# Revit family: LOROWERK 21712-050X
name_source: partatom
category: Sanitärinstallationen
revit_build: Autodesk Revit 2017 (Build: 20160225_1515(x64)
units: mm (PartAtom-declared; Revit-internal decimal feet)

## family parameters
Arbeitsebenenbasiert = Nein
Beim Laden mit Abzugskörper schneiden = Nein
Bemaßung runder Anschluss = Durchmesser verwenden
Gemeinsam genutzt = Nein
Immer vertikal = Ja
Raumberechnungspunkt = Nein
Teiletyp = Normal

## types (1)
- LOROWERK 21712-050X
    Abdichtung Grundkörper = mit Klemmflansch (Pressdichtungsflansch)
    Ablaufanschluss Text = mittig
    Anschluss an GLT, GA = Nein
    Begleitheizung = ohne Begleitheizung
    Beschreibung = LORO-DRAINLET DL Flachdachabläufe, einteilig
    Brandschutz mit Klasse R 120 nachrüstbar = Nein
    CONNECTOR0_DIAMETER_dZ_0r = 70 mm
    CONNECTOR0_dZ_00 = 12 mm  [stored 0.0393701 ft]
    CONNECTOR0_dZ_01 = 13 mm
    CONNECTOR0_ref_dZ = 13 mm
    CONNECTOR1_DIAMETER_dZ_0r = 50 mm
    CONNECTOR1_dZ_00 = 260 mm
    CONNECTOR1_dZ_01 = 30 mm
    CONNECTOR1_ref_dZ = 30 mm
    DATANORM = 21712.050X
    Einbaubreite [mm] Number = 260
    Einbautiefe [mm] Number = 260
    Elektrischer Anschluss YesNo = Nein
    Entwässerungsart = Freispiegel
    GTIN = 4038088094914
    HAN = 21712.050X
    HeinzeBIM = https://www.heinze.de
    Hersteller = LOROWERK K.H. Vahlbrauk GmbH & Co. KG
    Komplettartikel (Einteilig) aus Kombination (Mehrteileausführung) Ablaufgrundkörper und Aufsatzstück = Ja
    LOROWERK 21712.050X en Visibility = Ja
    Material Text = nicht rostender Stahl
    Mit/ohne Geruchsverschluss = ohne Geruchverschluss
    Nenndrucksystem Text = PN
    Nennmaß = 50
    Nennweitensystem Text = DN
    Potenzialausgleich (Erdungsanschluss) vorhanden = Nein
    Produktfamilie = LORO-DRAINLET DL Flachdachabläufe, einteilig
    Produktname = LORO-DL Notablauf, Edelstahl, Klemmflansch, senkr., 1-tlg., mit WD, DN50
    Sperrwasserhöhe [mm] Number = 35
    Stutzen-Ausführung = senkrecht
    Typ der Abläufe = Ablauf-Punktförmig
    Typname = LORO-DL Notablauf, Edelstahl, Klemmflansch, senkr., 1-tlg., mit WD, DN50
    VDIBSN = 0020010000010010000010010010010000000030020000000400000001
    Wärmedämmung Text = mit Wärmedämmung
    mit Blätter-/Kiesfang = Ja
    mit Schallentkopplung = Nein

note: [stored X ft] marks values corroborated as IEEE doubles in the binary element streams (Revit-internal decimal feet)
